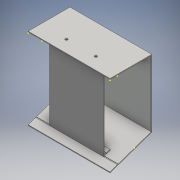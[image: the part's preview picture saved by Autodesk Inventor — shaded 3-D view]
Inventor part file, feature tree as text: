
AUTODESK INVENTOR PART (.ipt)
format: ipt  version: 2016 (Build 200138000, 138)  size: 256,512 bytes
history: native  units: mm
features: sketch x17, extrude x11, other x1
ambient origin geometry x8: Origin, YZ Plane, XZ Plane, XY Plane, X Axis, Y Axis, Z Axis, Center Point
bodies: Body1 (feature_tree)
feature tree (29):
  other  "Bryła1"
  extrude  "Wyciągnięcie proste1"  Depth=88.0mm
  extrude  "Wyciągnięcie proste2"  Depth=54.0mm
  sketch  "Szkic3"
  extrude  "Wyciągnięcie proste3"  Depth=9.0mm
  sketch  "Szkic5"
  sketch  "Szkic6"
  extrude  "Wyciągnięcie proste4"  Depth=1.0mm
  extrude  "Wyciągnięcie proste5"  Depth=54.0mm
  extrude  "Wyciągnięcie proste6"  Depth=12.391838mm
  extrude  "Wyciągnięcie proste7"  Depth=1.0mm
  extrude  "Wyciągnięcie proste8"  Depth=1.0mm
  sketch  "Szkic12"
  extrude  "Wyciągnięcie proste9"  Depth=1.0mm
  extrude  "Wyciągnięcie proste10"  Depth=100.0mm TaperAngle=0.0deg
  sketch  "Szkic15"
  sketch  "Szkic16"
  extrude  "Wyciągnięcie proste11"  Depth=10.0mm
  sketch  "Szkic1"
  sketch  "Szkic2"
  sketch  "Szkic4"
  sketch  "Szkic7"
  sketch  "Szkic8"
  sketch  "Szkic9"
  sketch  "Szkic10"
  sketch  "Szkic11"
  sketch  "Szkic13"
  sketch  "Szkic14"
  sketch  "Szkic17"
